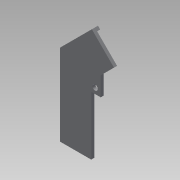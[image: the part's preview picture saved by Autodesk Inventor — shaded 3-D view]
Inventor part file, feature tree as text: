
AUTODESK INVENTOR PART (.ipt)
format: ipt  version: 2015 SP1 (Build 190203100, 203)  size: 114,176 bytes
history: native  units: mm
features: sketch x2, extrude x2, projected_geometry x1
ambient origin geometry x8: Origin, YZ Plane, XZ Plane, XY Plane, X Axis, Y Axis, Z Axis, Center Point
bodies: Body1 (feature_tree)
feature tree (5):
  sketch  "Sketch1"  dims[d18=2.0mm d19=0.0mm d20=15.0mm]
  extrude  "Extrusion3"  Depth=15.0mm
  extrude  "Extrusion4"  Depth=2.0mm
  sketch  "Sketch3"  dims[d21=90.0deg d22=2.0mm d23=15.0mm d24=90.0deg d25=2.0mm d26=15.0mm d27=45.0deg d28=2.0mm d29=7.5mm d30=2.0mm d31=2.0mm d32=0.0mm]
  projected_geometry  "Projected Loop1"
